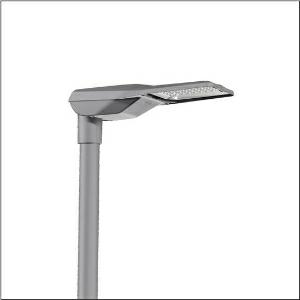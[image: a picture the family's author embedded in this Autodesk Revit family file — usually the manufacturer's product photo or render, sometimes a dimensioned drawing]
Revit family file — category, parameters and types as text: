
# Revit family: streetlight_sl_21_iq_mini___p1_0a_5xe2a41g08gb_a1a0
name_source: partatom
category: Lighting Fixtures
units: mm (PartAtom-declared; Revit-internal decimal feet)

## family parameters
Cut with Voids When Loaded = No
Host = Face
Light Source = No
Part Type = Normal
Room Calculation Point = No
Round Connector Dimension = Use Diameter
Shared = No

## types (1)
- --- (1 x LED, 5920 lm, 37.1 W, 4000K)
    Apparent Load = 37 VA
    CIE Flux Codes = 21 50 90 100 100
    Color Rendering = 70
    Color Temperature = 4000K
    Default Elevation = 1800 mm
    Description = Streetlight SL 21 iQ mini, mast luminaire, primary light control with lens, of PMMA, primary optical cover: cover, of toughened safety glass, transparent, light distribution: P1.0a, light emission: direct distribution, primary light characteristic: asymmetric, installation type: post-top, side-entry, LED, High Power LED, rated luminous flux: 5.920lm, luminous efficacy: 160lm/W, light colour: 740, colour temperature: 4000K, control gear: iQ Street-Remote, control: Street-Remote, Auto-Match, Temp-Guard, Lumen-Switch, Night-Set, Smart-Wire, Light-Fading, Desk-Remote (wireless, voltage-free reading and setting of iQ features in the workshop via application-optimized NFC function/RFID function), optimised constant luminous flux control (CLO 2.0), pre-setting: linear dimming characteristic, mains connection: 220..240V, AC, 50/60Hz, start of lifetime: 37W, end of service life: 39W, reduction: 18W, luminaire housing, of diecast aluminium, powder-coated, Siteco® metallic grey (DB 702S), corrosivity category C5 mid according to DIN EN ISO 12944, please order mast flange separately, inclination adjustable: 0°, 5°, 10°, 15°, sealing non-destructively replaceable, multi-level sealing system, length: 628mm, width: 235mm, height: 110mm, mast flange for spigot size: 42mm (side-entry): 5XC10008XM4, 60/48mm (side-entry/post-top): 5XC10108XM2, 76/60mm (side-entry/post-top): 5XC10108XM1, mounting height: 4..8m, protection rating (complete): IP66, insulation class (complete): insulation class II (safety insulation), certification: CE, ENEC, ENEC+, VDE, impact resistance: IK10, permissible operating ambient temperature for outdoor applications: -40..+50°C, standard-compliant lighting for roads and squares, packaging unit: 1 piece

Light Distribution: P1.0a
    Height = 110 mm
    Lamp = 1 x LED
    Lamp Light Flux = 5920 lm
    Lamp Power = 37.1 W
    Lamp count = 1
    Length = 625 mm
    Luminous efficacy = 160 lm/W
    Manufacturer = Siteco
    ModVariant = No
    Model = 5XE2A41G08GB
    Number of Poles = 1
    OnlyDefault = Yes
    Power Factor = 1
    Product Name = Streetlight SL 21 iQ mini | P1.0a
    Product group = mast luminaire | pylon top
    ProductGroupID = 6100
    Protection Class = Protection class II
    Protection Degree = IP 66
    RLX_Detail_Level = 1
    RLX_Emergency_Light_Flux = 0 lm
    RLX_Emergency_Type = 0
    RLX_Emergency_Type_DB = No
    RlxData = <blob elided: 37573 chars, md5=9edb9d47>
    Socket = socket
    Standby Power = 0 W
    System Light Flux = 5920 lm
    System Power = 37 W
    Type Comments = factory setting: luminous flux: 100 % | dim-lin: 254 | 385 mA
    Type Image = l_1003519.jpg
    URL = http://relux.com
    VarID = @adj_208039
    Voltage = 0 V
    Weight = 0.00 kg
    Width = 234 mm

## geometry (parser evidence)
native form markers: Blend x4, Sweep x10
no freeform markers — native parametric forms only
